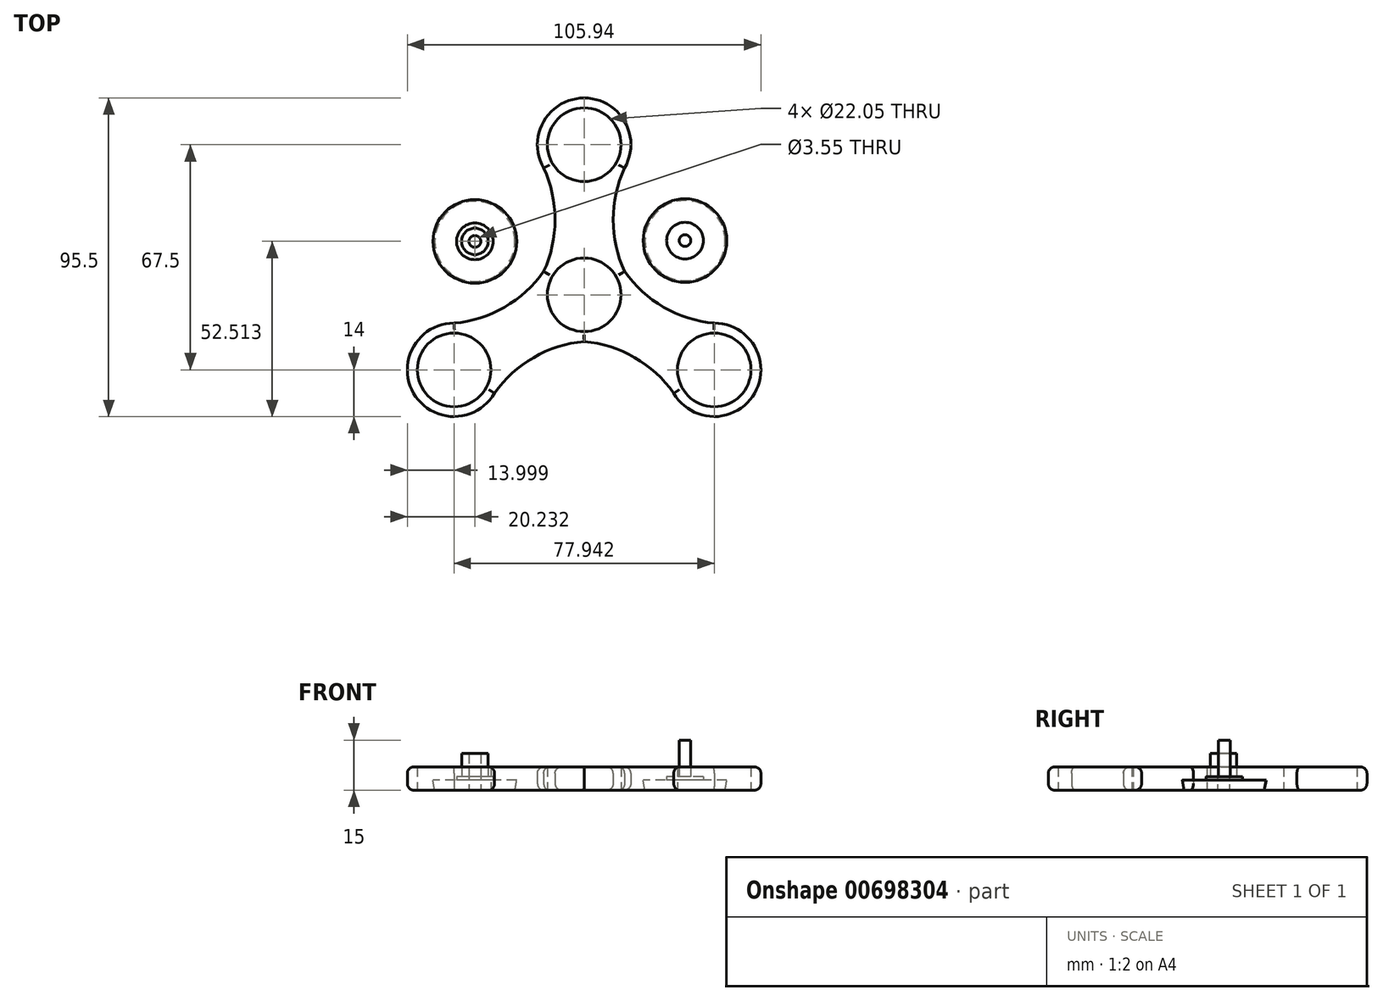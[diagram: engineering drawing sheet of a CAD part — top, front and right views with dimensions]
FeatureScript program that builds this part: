
annotation { "Feature Type Name" : "Feature", "Feature Type Description" : "" }
export const myFeature = defineFeature(function(context is Context, id is Id, definition is map)
    precondition{}
    {
        {
            var Q0;
            Q0=qCreatedBy(makeId("Top.planeOp"),FACE);
            var sketch = newSketch(context, id + "F0", { "sketchPlane" : qUnion([Q0])});
            skCircle(sketch, "E0", {"center": v(0, 0) * mm, "radius": 11.03 * mm});
            skCircle(sketch, "E1", {"center": v(0, 45) * mm, "radius": 11.03 * mm});
            skArc(sketch, "E2", {"start": v(12.12, 38) * mm, "mid": v(0, 59) * mm, "end": v(-12.12, 38) * mm});
            skArc(sketch, "E3", {"start": v(-12.12, 7) * mm, "mid": v(0, -14) * mm, "end": v(12.12, 7) * mm});
            skArc(sketch, "E4", {"start": v(-12.12, 7) * mm, "mid": v(-8.72, 22.5) * mm, "end": v(-12.12, 38) * mm});
            skArc(sketch, "E5", {"start": v(12.12, 38) * mm, "mid": v(8.72, 22.5) * mm, "end": v(12.12, 7) * mm});
            skSolve(sketch);
        }
        {
            var Q0;
            Q0=makeQuery(id+"F0.imprint","IMPRINT",FACE,{"disambiguationData":[TD([[makeQuery(id+"F0.imprint","IMPRINT",EDGE,{"derivedFrom":sQuery(id+"F0.wireOp",EDGE,"E0")}),-1.0]])]});
            extrude(context, id + "F1", {"entities" : qUnion([Q0]), "depth" : 7 * mm, "offsetDistance" : 25 * mm});
        }
        {
            var Q0;
            Q0=makeQuery(id+"F1.opExtrude","CAP_EDGE",EDGE,{"disambiguationData":[OSD([sQuery(id+"F0.wireOp",EDGE,"E4")])],"isStart":false});
            var Q1;
            Q1=makeQuery(id+"F1.opExtrude","CAP_EDGE",EDGE,{"disambiguationData":[OSD([sQuery(id+"F0.wireOp",EDGE,"E4")])],"isStart":true});
            var Q2;
            Q2=makeQuery(id+"F1.opExtrude","CAP_EDGE",EDGE,{"disambiguationData":[OSD([sQuery(id+"F0.wireOp",EDGE,"E2")])],"isStart":false});
            var Q3;
            Q3=makeQuery(id+"F1.opExtrude","CAP_EDGE",EDGE,{"disambiguationData":[OSD([sQuery(id+"F0.wireOp",EDGE,"E2")])],"isStart":true});
            var Q4;
            Q4=makeQuery(id+"F1.opExtrude","CAP_EDGE",EDGE,{"disambiguationData":[OSD([sQuery(id+"F0.wireOp",EDGE,"E5")])],"isStart":false});
            var Q5;
            Q5=makeQuery(id+"F1.opExtrude","CAP_EDGE",EDGE,{"disambiguationData":[OSD([sQuery(id+"F0.wireOp",EDGE,"E5")])],"isStart":true});
            fillet(context, id + "F2", {"entities" : qUnion([Q0, Q1, Q2, Q3, Q4, Q5]), "radius" : 2 * mm, "tangentPropagation" : true, "allowEdgeOverflow" : false});
        }
        {
            var Q0;
            Q0=makeQuery(id+"F1.opExtrude","SWEPT_BODY",BODY,{"disambiguationData":[OSD([sQuery(id+"F0.wireOp",EDGE,"E0"),sQuery(id+"F0.wireOp",EDGE,"E1"),sQuery(id+"F0.wireOp",EDGE,"E2"),sQuery(id+"F0.wireOp",EDGE,"E3"),sQuery(id+"F0.wireOp",EDGE,"E4"),sQuery(id+"F0.wireOp",EDGE,"E5")])]});
            var Q1;
            Q1=makeQuery(id+"F1.opExtrude","CAP_EDGE",EDGE,{"disambiguationData":[OSD([sQuery(id+"F0.wireOp",EDGE,"E0")])],"isStart":false});
            circularPattern(context, id + "F3", {"operationType" : NewBodyOperationType.ADD, "entities" : qUnion([Q0]), "axis" : qUnion([Q1]), "angle" : 360 * degree, "instanceCount" : 3, "equalSpace" : true});
        }
        {
            var Q0;
            {var subQ1=sQuery(id+"F0.wireOp",EDGE,"E4");var subQ2=sQuery(id+"F0.wireOp",EDGE,"E3");Q0=makeQuery(id+"F3.boolean.opBoolean","SPLIT",EDGE,{"disambiguationData":[TD([makeQuery(id+"F3.opPattern","COPY",FACE,{"derivedFrom":makeQuery(id+"F2.opFillet","BLEND_FACE",FACE,{"disambiguationData":[OSD([subQ1]),TDD([makeQuery(id+"F1.opExtrude","CAP_EDGE",EDGE,{"disambiguationData":[OSD([subQ1])],"isStart":false})])]}),"instanceName":"1"})])],"derivedFrom":makeQuery(id+"F1.opExtrude","CAP_EDGE",EDGE,{"disambiguationData":[OSD([subQ2])],"isStart":false})});}
            var Q1;
            {var subQ1=sQuery(id+"F0.wireOp",EDGE,"E4");var subQ2=sQuery(id+"F0.wireOp",EDGE,"E3");Q1=makeQuery(id+"F3.boolean.opBoolean","SPLIT",EDGE,{"disambiguationData":[TD([makeQuery(id+"F3.opPattern","COPY",FACE,{"derivedFrom":makeQuery(id+"F2.opFillet","BLEND_FACE",FACE,{"disambiguationData":[OSD([subQ1]),TDD([makeQuery(id+"F1.opExtrude","CAP_EDGE",EDGE,{"disambiguationData":[OSD([subQ1])],"isStart":true})])]}),"instanceName":"1"})])],"derivedFrom":makeQuery(id+"F1.opExtrude","CAP_EDGE",EDGE,{"disambiguationData":[OSD([subQ2])],"isStart":true})});}
            var Q2;
            {var subQ0=sQuery(id+"F0.wireOp",EDGE,"E5");var subQ2=sQuery(id+"F0.wireOp",EDGE,"E3");Q2=makeQuery(id+"F3.boolean.opBoolean","SPLIT",EDGE,{"disambiguationData":[TD([makeQuery(id+"F2.opFillet","BLEND_FACE",FACE,{"disambiguationData":[OSD([subQ0]),TDD([makeQuery(id+"F1.opExtrude","CAP_EDGE",EDGE,{"disambiguationData":[OSD([subQ0])],"isStart":false})])]})])],"derivedFrom":makeQuery(id+"F1.opExtrude","CAP_EDGE",EDGE,{"disambiguationData":[OSD([subQ2])],"isStart":false})});}
            var Q3;
            {var subQ0=sQuery(id+"F0.wireOp",EDGE,"E5");var subQ2=sQuery(id+"F0.wireOp",EDGE,"E3");Q3=makeQuery(id+"F3.boolean.opBoolean","SPLIT",EDGE,{"disambiguationData":[TD([makeQuery(id+"F2.opFillet","BLEND_FACE",FACE,{"disambiguationData":[OSD([subQ0]),TDD([makeQuery(id+"F1.opExtrude","CAP_EDGE",EDGE,{"disambiguationData":[OSD([subQ0])],"isStart":true})])]})])],"derivedFrom":makeQuery(id+"F1.opExtrude","CAP_EDGE",EDGE,{"disambiguationData":[OSD([subQ2])],"isStart":true})});}
            var Q4;
            {var subQ1=sQuery(id+"F0.wireOp",EDGE,"E4");var subQ2=sQuery(id+"F0.wireOp",EDGE,"E3");Q4=makeQuery(id+"F3.boolean.opBoolean","SPLIT",EDGE,{"disambiguationData":[TD([makeQuery(id+"F2.opFillet","BLEND_FACE",FACE,{"disambiguationData":[OSD([subQ1]),TDD([makeQuery(id+"F1.opExtrude","CAP_EDGE",EDGE,{"disambiguationData":[OSD([subQ1])],"isStart":false})])]})])],"derivedFrom":makeQuery(id+"F1.opExtrude","CAP_EDGE",EDGE,{"disambiguationData":[OSD([subQ2])],"isStart":false})});}
            var Q5;
            {var subQ1=sQuery(id+"F0.wireOp",EDGE,"E4");var subQ2=sQuery(id+"F0.wireOp",EDGE,"E3");Q5=makeQuery(id+"F3.boolean.opBoolean","SPLIT",EDGE,{"disambiguationData":[TD([makeQuery(id+"F2.opFillet","BLEND_FACE",FACE,{"disambiguationData":[OSD([subQ1]),TDD([makeQuery(id+"F1.opExtrude","CAP_EDGE",EDGE,{"disambiguationData":[OSD([subQ1])],"isStart":true})])]})])],"derivedFrom":makeQuery(id+"F1.opExtrude","CAP_EDGE",EDGE,{"disambiguationData":[OSD([subQ2])],"isStart":true})});}
            fillet(context, id + "F4", {"entities" : qUnion([Q0, Q1, Q2, Q3, Q4, Q5]), "radius" : 2 * mm, "tangentPropagation" : true, "allowEdgeOverflow" : false});
        }
        {
            var Q0;
            Q0=qCreatedBy(makeId("Top.planeOp"),FACE);
            var sketch = newSketch(context, id + "F5", { "sketchPlane" : qUnion([Q0])});
            skCircle(sketch, "E6", {"center": v(-32.74, 16.01) * mm, "radius": 3.98 * mm});
            skCircle(sketch, "E7", {"center": v(-32.74, 16.01) * mm, "radius": 5.5 * mm});
            skCircle(sketch, "E8", {"center": v(-32.74, 16.01) * mm, "radius": 12 * mm});
            skCircle(sketch, "E9", {"center": v(30.22, 16.25) * mm, "radius": 1.75 * mm});
            skCircle(sketch, "E10", {"center": v(30.22, 16.25) * mm, "radius": 5.5 * mm});
            skCircle(sketch, "E11", {"center": v(30.22, 16.25) * mm, "radius": 12 * mm});
            skCircle(sketch, "E12", {"center": v(-32.74, 16.01) * mm, "radius": 1.77 * mm});
            skSolve(sketch);
        }
        {
            var Q0;
            Q0=makeQuery(id+"F5.imprint","IMPRINT",FACE,{"disambiguationData":[TD([[makeQuery(id+"F5.imprint","IMPRINT",EDGE,{"derivedFrom":sQuery(id+"F5.wireOp",EDGE,"E7")}),-1.0]])]});
            extrude(context, id + "F6", {"entities" : qUnion([Q0]), "depth" : 3 * mm, "offsetDistance" : 25 * mm, "hasDraft" : true, "draftAngle" : 10 * degree});
        }
        {
            var Q0;
            Q0=makeQuery(id+"F5.imprint","IMPRINT",FACE,{"disambiguationData":[TD([[makeQuery(id+"F5.imprint","IMPRINT",EDGE,{"derivedFrom":sQuery(id+"F5.wireOp",EDGE,"E6")}),-1.0]])]});
            extrude(context, id + "F7", {"entities" : qUnion([Q0]), "operationType" : NewBodyOperationType.ADD, "depth" : 4 * mm, "offsetDistance" : 25 * mm});
        }
        {
            var Q0;
            Q0=makeQuery(id+"F5.imprint","IMPRINT",FACE,{"disambiguationData":[TD([[makeQuery(id+"F5.imprint","IMPRINT",EDGE,{"derivedFrom":sQuery(id+"F5.wireOp",EDGE,"E6")}),1.0]])]});
            extrude(context, id + "F8", {"entities" : qUnion([Q0]), "operationType" : NewBodyOperationType.ADD, "depth" : 11 * mm, "offsetDistance" : 25 * mm});
        }
        {
            var Q0;
            Q0=makeQuery(id+"F5.imprint","IMPRINT",FACE,{"disambiguationData":[TD([[makeQuery(id+"F5.imprint","IMPRINT",EDGE,{"derivedFrom":sQuery(id+"F5.wireOp",EDGE,"E10")}),-1.0]])]});
            extrude(context, id + "F9", {"entities" : qUnion([Q0]), "depth" : 3 * mm, "offsetDistance" : 25 * mm, "hasDraft" : true, "draftAngle" : 10 * degree});
        }
        {
            var Q0;
            Q0=makeQuery(id+"F5.imprint","IMPRINT",FACE,{"disambiguationData":[TD([[makeQuery(id+"F5.imprint","IMPRINT",EDGE,{"derivedFrom":sQuery(id+"F5.wireOp",EDGE,"E9")}),-1.0]])]});
            extrude(context, id + "F10", {"entities" : qUnion([Q0]), "operationType" : NewBodyOperationType.ADD, "depth" : 4 * mm, "offsetDistance" : 25 * mm});
        }
        {
            var Q0;
            Q0=makeQuery(id+"F5.imprint","IMPRINT",FACE,{"disambiguationData":[TD([[makeQuery(id+"F5.imprint","IMPRINT",EDGE,{"derivedFrom":sQuery(id+"F5.wireOp",EDGE,"E9")}),1.0]])]});
            extrude(context, id + "F11", {"entities" : qUnion([Q0]), "operationType" : NewBodyOperationType.ADD, "depth" : 15 * mm, "offsetDistance" : 25 * mm});
        }
    });
